# Revit family: 543006-430016
name_source: partatom
category: Plumbing Fixtures
revit_build: Autodesk Revit 2015 (Build: 20140606_1530(x64)
units: mm (PartAtom-declared; Revit-internal decimal feet)

## types (1)
- Type 1
    Category = Urinal valve
    Color = Black
    DLB090010 = Stainless Steel
    Description = French manufacturer Delabie is a leader in the European sanitary ware market for non-domestic places. Water controls, solutions for disabled people, sanitary ware, for schools, leisure centres, offices, hospitals, airports…
    Diameter = 19 mm  [stored 0.062336 ft]
    Features = Frame system W. 420mm for urinals: Black epoxy coated steel frame for exposed installation. Fixes to load-bearing floors and walls with supplied anchoring bolts. Adjustable bracket 100 - 280mm. Frame height can be adjusted 0 - 200mm. Ø 50mm soil pipe with waterproof seal. Delivered pre-mounted. Conforms to standard NF D12-208. Compatible with wall finishes 13 - 120mm.  Fitted with F½" electronic valve: Battery-operated with 123 6V Lithium battery Bright stainless steel plate 145 x 145mm with integrated electronics. Shockproof infrared presence detection sensor. Waterproof recessing housing. Activates after 10 seconds of presence. 3 programmes (rinsing volume can be set according to the type of urinal). High frequency mode (exclusive to DELABIE). Flow rate pre-set at 0.15 lps. at 3 bar, can be adjusted. Hygienic duty flush every 12 or 24 hours (or Off) after last use: prevents backflow. Order a connection with Ø 35mm connection washer (for standard urinals) or ½" brass connection (for urinals with flexible supply).
    Finish = Bright polished
    FlowRate = 0,15 lps at 3 bar
    IntegralAccessories = Neck tube
    IntegralAccessoryOptions = Stainless Steel urinal
    Manufacturer = DELABIE
    ManufacturerName = DELABIE
    Material = Epoxy steel and stainless steel
    Model = TEMPOFIX 3 with TEMPOMATIC 4
    Model number = 543006 + 430016
    Name = 543006 + 430016
    NominalHeight = 98.5 - 138.5 cm
    NominalLength = 1.3 - 12
    NominalWidth = 43 cm
    Operation = Electronic valve
    Polantis code = DLB090010
    ProductInformation = http://www.delabie.com
    SerialNumber = 3456330169691 + 3456330166980
    URL = http://www.delabie.com
    WarrantyDescription = Any manufacturing defect
    WarrantyDurationUnit = 10 years

note: [stored X ft] marks values corroborated as IEEE doubles in the binary element streams (Revit-internal decimal feet)

## geometry (parser evidence)
native form markers: Sweep x23
no freeform markers — native parametric forms only
